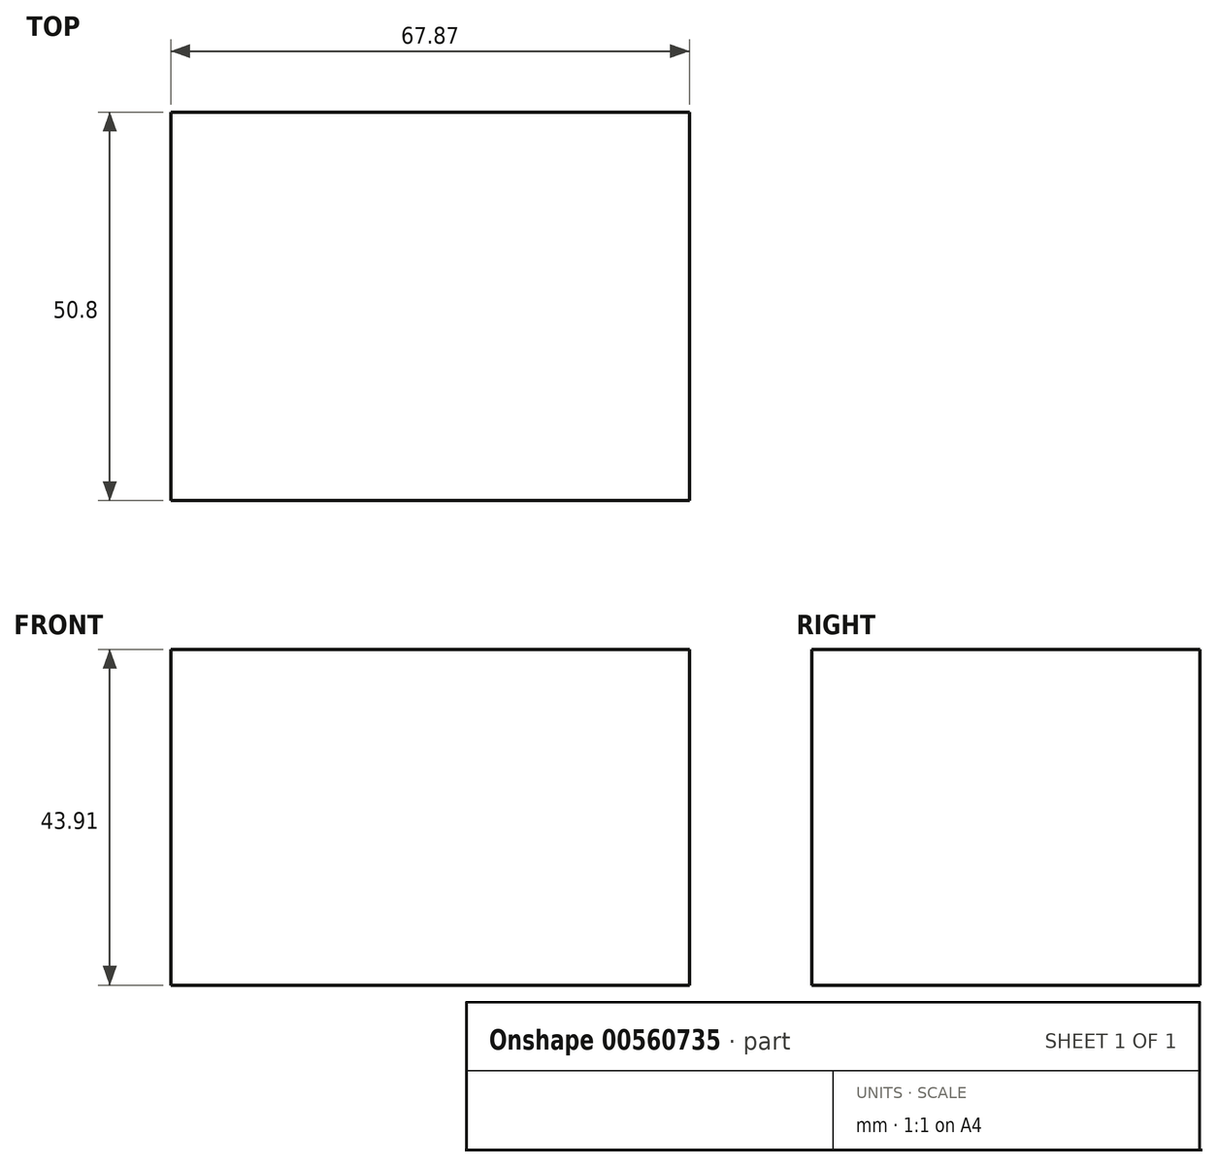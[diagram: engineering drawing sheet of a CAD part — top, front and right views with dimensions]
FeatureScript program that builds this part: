
annotation { "Feature Type Name" : "Feature", "Feature Type Description" : "" }
export const myFeature = defineFeature(function(context is Context, id is Id, definition is map)
    precondition{}
    {
        {
            var Q0;
            Q0=qCreatedBy(makeId("Front.planeOp"),FACE);
            var sketch = newSketch(context, id + "F0", { "sketchPlane" : qUnion([Q0])});
            skLineSegment(sketch, "E0.bottom", {"start": v(0, 0) * mm, "end": v(67.87, 0) * mm});
            skLineSegment(sketch, "E0.top", {"start": v(0, -43.9) * mm, "end": v(67.87, -43.9) * mm});
            skLineSegment(sketch, "E0.left", {"start": v(0, 0) * mm, "end": v(0, -43.9) * mm});
            skLineSegment(sketch, "E0.right", {"start": v(67.87, 0) * mm, "end": v(67.87, -43.9) * mm});
            skSolve(sketch);
        }
        {
            var Q0;
            Q0=makeQuery(id+"F0.imprint","IMPRINT",FACE,{"disambiguationData":[TD([[makeQuery(id+"F0.imprint","IMPRINT",EDGE,{"derivedFrom":sQuery(id+"F0.wireOp",EDGE,"E0.bottom")}),-1.0]])]});
            extrude(context, id + "F1", {"entities" : qUnion([Q0]), "depth" : 50.8 * mm, "offsetDistance" : 25.4 * mm});
        }
    });
